# Revit family: sh-1289-s
name_source: partatom
category: Lighting Fixtures
revit_build: Autodesk Revit 2017 (Build: 20160225_1515(x64)
units: mm (PartAtom-declared; Revit-internal decimal feet)

## family parameters
Always vertical = Yes
Cut with Voids When Loaded = No
Light Source = Yes
OmniClass Number = 23.80.70.00
OmniClass Title = Lighting
Part Type = Normal
Room Calculation Point = No
Round Connector Dimension = Use Diameter
Shared = No
Work Plane-Based = No

## types (3) — shared parameters
Color Filter = 16777215
Color Temperature(CT) = 2000K-3000K-6500K
Depth = 10.0 cm
Dimming Lamp Color Temperature Shift = <None>
Emit Shape Visible in Rendering = No
Emit from Circle Diameter = 61.0 cm
Flicker = FREE Flicker
IP = IP65
Instalation = inground
Lamp = LED
Manufacturer = SHOA
Model = SH-1289-s
Photometric Web File = CFAL4029 -15W .ies
Protection class = Class I
Tilt Angle = -90.00°
Type medule = Power Led
URL = https://www.shoaco.com
Voltage/Frequency = 230V-50HZ
Wattage. = 3.4w
body color = Black
body material = Aluminium
color rendering index(CRI) = 80
consumption current = 32mA
cutting diameter = 8.0 cm
length = 9.0 cm
website = www.shoaco.com
weight = 9.0 cm

## type names (no varying parameters)
- SH-1289-s(Aluminium body-2000K-LED)
- SH-1289-s(Aluminium body-3000K-LED)
- SH-1289-s(Aluminium body-6500K-LED)

## geometry (parser evidence)
native form markers: Sweep x3
no freeform markers — native parametric forms only
